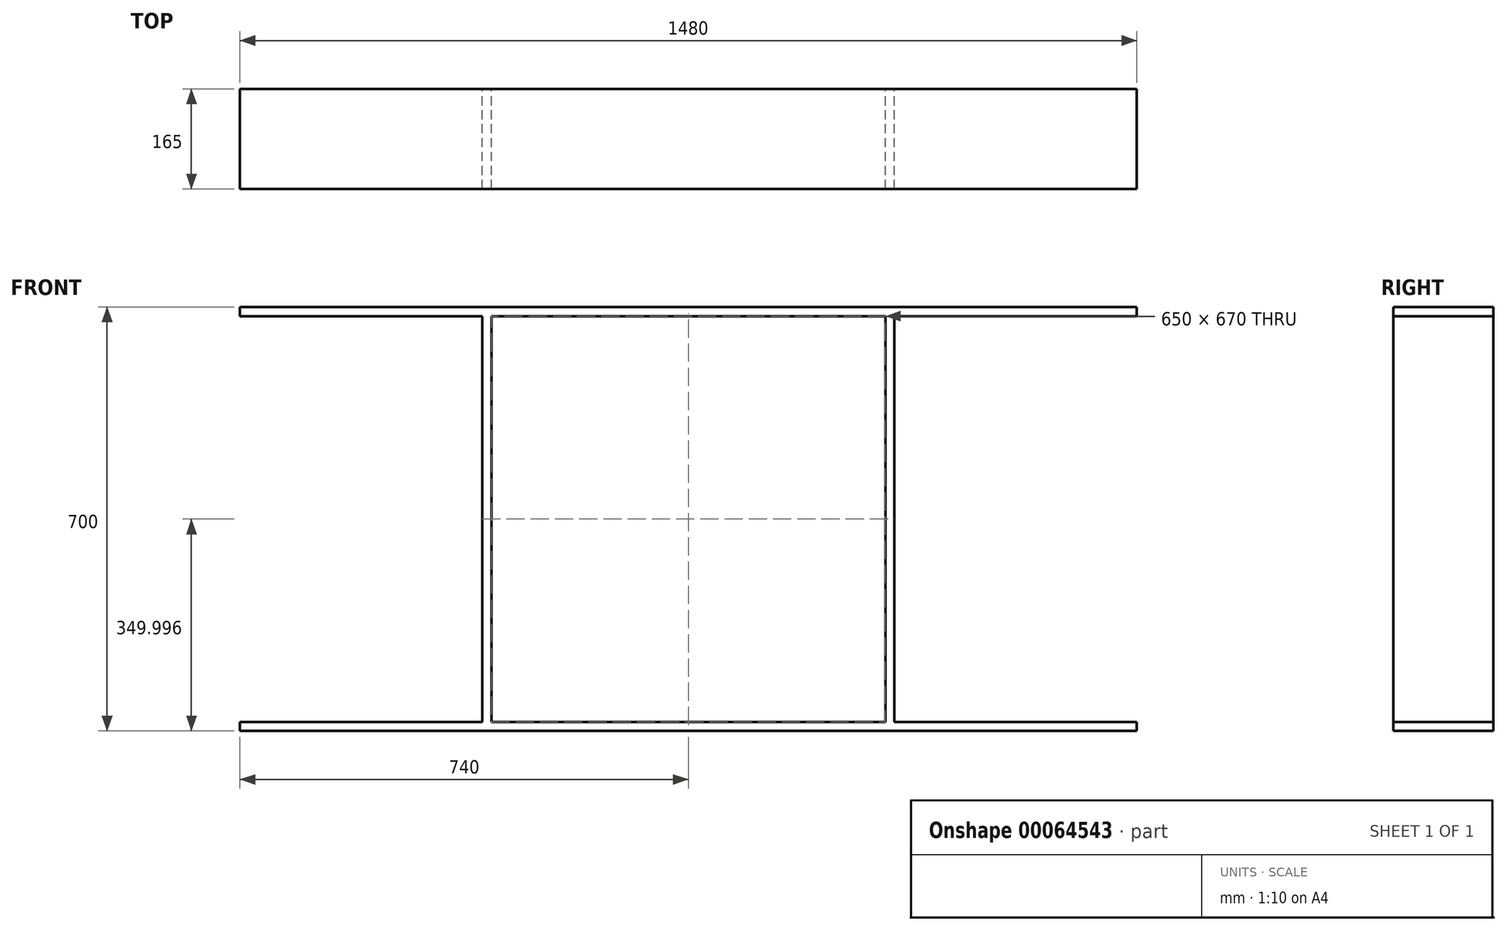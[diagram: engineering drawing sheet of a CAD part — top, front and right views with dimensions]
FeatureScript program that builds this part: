
annotation { "Feature Type Name" : "Feature", "Feature Type Description" : "" }
export const myFeature = defineFeature(function(context is Context, id is Id, definition is map)
    precondition{}
    {
        {
            var Q0;
            Q0=qCreatedBy(makeId("Front.planeOp"),FACE);
            var sketch = newSketch(context, id + "F0", { "sketchPlane" : qUnion([Q0])});
            skLineSegment(sketch, "E0", {"start": v(-780.51, 421.22) * mm, "end": v(-780.51, 436.22) * mm});
            skLineSegment(sketch, "E1", {"start": v(-780.51, 436.22) * mm, "end": v(699.49, 436.22) * mm});
            skLineSegment(sketch, "E2", {"start": v(699.49, 436.22) * mm, "end": v(699.49, 421.22) * mm});
            skLineSegment(sketch, "E3", {"start": v(699.49, 421.22) * mm, "end": v(299.49, 421.22) * mm});
            skLineSegment(sketch, "E4", {"start": v(299.49, 421.22) * mm, "end": v(299.49, -248.78) * mm});
            skLineSegment(sketch, "E5", {"start": v(299.49, -248.78) * mm, "end": v(699.49, -248.78) * mm});
            skLineSegment(sketch, "E6", {"start": v(699.49, -248.78) * mm, "end": v(699.49, -263.78) * mm});
            skLineSegment(sketch, "E7", {"start": v(699.49, -263.78) * mm, "end": v(-780.51, -263.78) * mm});
            skLineSegment(sketch, "E8", {"start": v(-780.51, -263.78) * mm, "end": v(-780.51, -248.78) * mm});
            skLineSegment(sketch, "E9", {"start": v(-780.51, -248.78) * mm, "end": v(-380.51, -248.78) * mm});
            skLineSegment(sketch, "E10", {"start": v(-380.51, -248.78) * mm, "end": v(-380.51, 421.22) * mm});
            skLineSegment(sketch, "E11", {"start": v(-380.51, 421.22) * mm, "end": v(-780.51, 421.22) * mm});
            skLineSegment(sketch, "E12", {"start": v(-365.51, -248.78) * mm, "end": v(-365.51, 421.22) * mm});
            skLineSegment(sketch, "E13", {"start": v(-365.51, 421.22) * mm, "end": v(284.49, 421.22) * mm});
            skLineSegment(sketch, "E14", {"start": v(284.49, 421.22) * mm, "end": v(284.49, -248.78) * mm});
            skLineSegment(sketch, "E15", {"start": v(284.49, -248.78) * mm, "end": v(-365.51, -248.78) * mm});
            skSolve(sketch);
        }
        {
            var Q0;
            Q0=makeQuery(id+"F0.imprint","IMPRINT",FACE,{"disambiguationData":[TD([[makeQuery(id+"F0.imprint","IMPRINT",EDGE,{"derivedFrom":sQuery(id+"F0.wireOp",EDGE,"E0")}),-1.0]])]});
            extrude(context, id + "F1", {"entities" : qUnion([Q0]), "depth" : 165 * mm});
        }
    });
